# Revit family: QF_BOURGEAT_Transtherm_Fours_mobiles_10GN1_1
name_source: partatom
category: Equipement spécialisé
revit_build: Autodesk Revit 2015 (Build: 20140606_1530(x64)
units: mm (PartAtom-declared; Revit-internal decimal feet)

## types (4) — shared parameters
Certification = NF alimentaire
Charge max = 40.00 kg
Consommation énergétique = 6.06Kwh/h
Fabricant = BOURGEAT
Fréquence = 50 Hz
Hauteur hors tout = 1320 mm
Intensité nominale = 22 A
Longueur hors tout = 744 mm  [stored 2.44094 ft]
Nature isolant = Laine_de_roche(60mm)
Phase = 3
Poids net à vide = 80.00 kg
Profondeur hors tout = 782 mm
Puissance électrique  = 8700 W
Spécification du Fabricant = TRANS'THERM
Tension = 400 V
URL catalogue = http://www.bourgeat.fr

## per-type parameters (varying)
| type | Indice de protection |
| 893210 | IP25 |
| 893210 + 897500 | IP25 |
| 893910 | IP55 |
| 893910 + 897500 | IP25 |

note: column(s) folded — value = type name in every type: Modèle, Type_de_modele

note: [stored X ft] marks values corroborated as IEEE doubles in the binary element streams (Revit-internal decimal feet)
